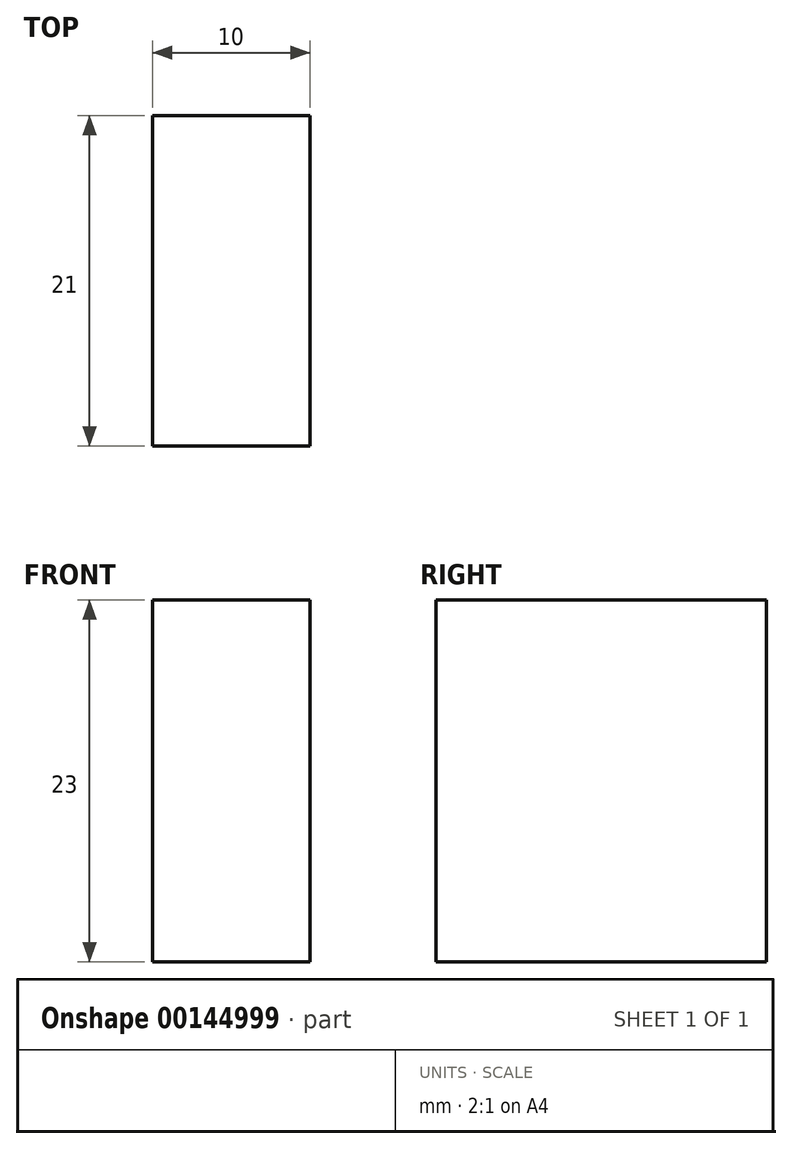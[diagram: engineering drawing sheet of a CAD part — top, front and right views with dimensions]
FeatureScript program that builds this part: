
annotation { "Feature Type Name" : "Feature", "Feature Type Description" : "" }
export const myFeature = defineFeature(function(context is Context, id is Id, definition is map)
    precondition{}
    {
        {
            var Q0;
            Q0=qCreatedBy(makeId("Top.planeOp"),FACE);
            var sketch = newSketch(context, id + "F0", { "sketchPlane" : qUnion([Q0])});
            skLineSegment(sketch, "E0.bottom", {"start": v(-5, 10.5) * mm, "end": v(5, 10.5) * mm});
            skLineSegment(sketch, "E0.top", {"start": v(-5, -10.5) * mm, "end": v(5, -10.5) * mm});
            skLineSegment(sketch, "E0.left", {"start": v(-5, 10.5) * mm, "end": v(-5, -10.5) * mm});
            skLineSegment(sketch, "E0.right", {"start": v(5, 10.5) * mm, "end": v(5, -10.5) * mm});
            skSolve(sketch);
        }
        {
            var Q0;
            Q0=makeQuery(id+"F0.imprint","IMPRINT",FACE,{"disambiguationData":[TD([[makeQuery(id+"F0.imprint","IMPRINT",EDGE,{"derivedFrom":sQuery(id+"F0.wireOp",EDGE,"E0.bottom")}),-1.0]])]});
            extrude(context, id + "F1", {"entities" : qUnion([Q0]), "depth" : 23 * mm});
        }
    });
